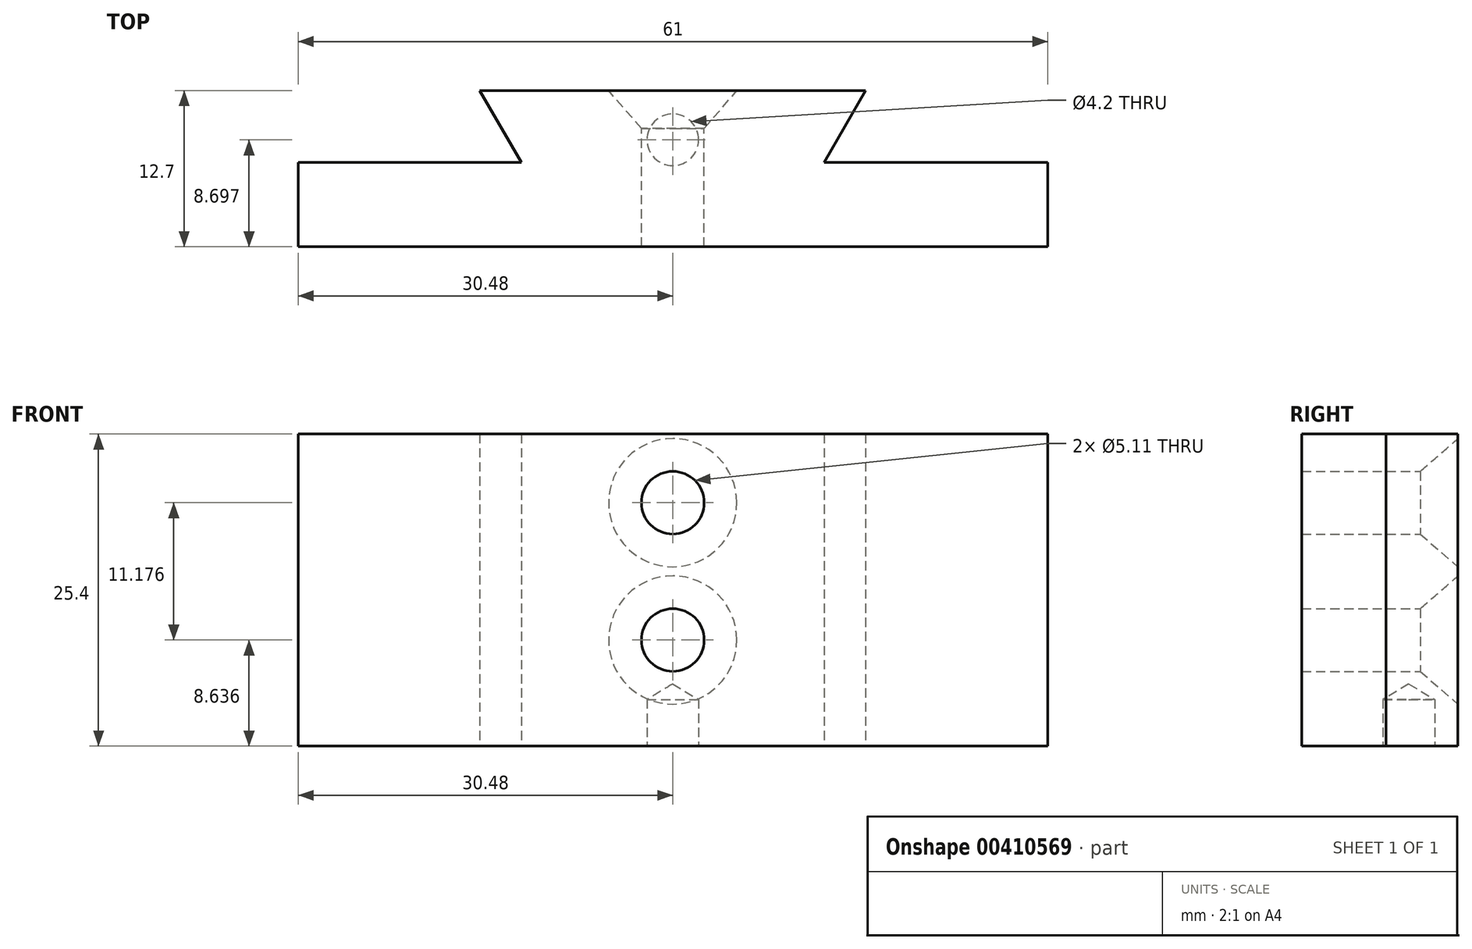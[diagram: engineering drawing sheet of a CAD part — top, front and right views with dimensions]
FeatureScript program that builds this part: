
annotation { "Feature Type Name" : "Feature", "Feature Type Description" : "" }
export const myFeature = defineFeature(function(context is Context, id is Id, definition is map)
    precondition{}
    {
        {
            var Q0;
            Q0=qCreatedBy(makeId("Top.planeOp"),FACE);
            var sketch = newSketch(context, id + "F0", { "sketchPlane" : qUnion([Q0])});
            skLineSegment(sketch, "E0", {"start": v(0, 8.03) * mm, "end": v(-15.7, 8.03) * mm});
            skLineSegment(sketch, "E1.MirrorCS", {"start": v(0, 8.03) * mm, "end": v(15.7, 8.03) * mm});
            skLineSegment(sketch, "E2", {"start": v(0, 2.19) * mm, "end": v(-30.48, 2.19) * mm});
            skLineSegment(sketch, "E3.MirrorCS", {"start": v(0, 2.19) * mm, "end": v(30.48, 2.19) * mm});
            skLineSegment(sketch, "E4", {"start": v(-15.7, 8.03) * mm, "end": v(-12.33, 2.19) * mm});
            skLineSegment(sketch, "E5.MirrorCS", {"start": v(15.7, 8.03) * mm, "end": v(12.33, 2.19) * mm});
            skLineSegment(sketch, "E6.bottom", {"start": v(-30.48, 2.19) * mm, "end": v(30.52, 2.19) * mm});
            skLineSegment(sketch, "E6.top", {"start": v(-30.48, -4.67) * mm, "end": v(30.52, -4.67) * mm});
            skLineSegment(sketch, "E6.left", {"start": v(-30.48, 2.19) * mm, "end": v(-30.48, -4.67) * mm});
            skLineSegment(sketch, "E6.right", {"start": v(30.52, 2.19) * mm, "end": v(30.52, -4.67) * mm});
            skLineSegment(sketch, "E7", {"start": v(-17.76, 4.03) * mm, "end": v(19.96, 4.03) * mm, "construction": true});
            skPoint(sketch, "E8", {"position": v(0, 4.03) * mm});
            skSolve(sketch);
        }
        {
            var Q0;
            Q0 = qSketchRegion(id + "F0", true);
            extrude(context, id + "F1", {"entities" : qUnion([Q0]), "depth" : 25.4 * mm});
        }
        {
            var Q0;
            Q0=qCreatedBy(makeId("Top.planeOp"),FACE);
            var sketch = newSketch(context, id + "F2", { "sketchPlane" : qUnion([Q0])});
            skLineSegment(sketch, "E9", {"start": v(-33.8, 4.03) * mm, "end": v(32.14, 4.03) * mm, "construction": true});
            skPoint(sketch, "E10", {"position": v(0, 4.03) * mm});
            skSolve(sketch);
        }
        {
            var Q0;
            Q0=sQuery(id+"F2.wireOp",VERTEX,"E10");
            var Q1;
            Q1=makeQuery(id+"F1.opExtrude","SWEPT_BODY",BODY,{"disambiguationData":[OSD([sQuery(id+"F0.wireOp",EDGE,"E0"),sQuery(id+"F0.wireOp",EDGE,"E1.MirrorCS"),sQuery(id+"F0.wireOp",EDGE,"E4"),sQuery(id+"F0.wireOp",EDGE,"E5.MirrorCS"),sQuery(id+"F0.wireOp",EDGE,"E6.bottom"),sQuery(id+"F0.wireOp",EDGE,"E6.top"),sQuery(id+"F0.wireOp",EDGE,"E6.left"),sQuery(id+"F0.wireOp",EDGE,"E6.right")])]});
            hole(context, id + "F3", {"style" : HoleStyle.SIMPLE, "endStyle" : HoleEndStyle.BLIND, "oppositeDirection" : true, "standardTappedOrClearance" : lookupTablePath({ "standard" : "ISO", "engagement" : "75%", "pitch" : "0.8 mm", "size" : "M5", "type" : "Tapped" }), "standardBlindInLast" : lookupTablePath({ "standard" : "ISO", "engagement" : "75%", "pitch" : "0.8 mm", "size" : "M5", "type" : "Tapped" }), "holeDiameter" : 4.2 * mm, "showTappedDepth" : true, "holeDepth" : 3.8 * mm, "isTappedThrough" : true, "tappedDepth" : 3 * mm, "tapClearance" : 1, "startFromSketch" : true, "locations" : qUnion([Q0]), "scope" : qUnion([Q1]), "majorDiameter" : 5 * mm});
        }
        {
            var Q0;
            Q0=makeQuery(id+"F1.opExtrude","SWEPT_FACE",FACE,{"disambiguationData":[OSD([sQuery(id+"F0.wireOp",EDGE,"E0"),sQuery(id+"F0.wireOp",EDGE,"E1.MirrorCS")])]});
            var sketch = newSketch(context, id + "F4", { "sketchPlane" : qUnion([Q0])});
            skLineSegment(sketch, "E11", {"start": v(-27.44, 19.81) * mm, "end": v(30.95, 19.81) * mm, "construction": true});
            skLineSegment(sketch, "E12", {"start": v(-27.44, 8.64) * mm, "end": v(34.23, 8.64) * mm, "construction": true});
            skPoint(sketch, "E13", {"position": v(0, 19.81) * mm});
            skPoint(sketch, "E14", {"position": v(0, 8.64) * mm});
            skSolve(sketch);
        }
        {
            var Q0;
            Q0=sQuery(id+"F4.wireOp",VERTEX,"E13");
            var Q1;
            Q1=makeQuery(id+"F1.opExtrude","SWEPT_BODY",BODY,{"disambiguationData":[OSD([sQuery(id+"F0.wireOp",EDGE,"E0"),sQuery(id+"F0.wireOp",EDGE,"E1.MirrorCS"),sQuery(id+"F0.wireOp",EDGE,"E4"),sQuery(id+"F0.wireOp",EDGE,"E5.MirrorCS"),sQuery(id+"F0.wireOp",EDGE,"E6.bottom"),sQuery(id+"F0.wireOp",EDGE,"E6.top"),sQuery(id+"F0.wireOp",EDGE,"E6.left"),sQuery(id+"F0.wireOp",EDGE,"E6.right")])]});
            hole(context, id + "F5", {"style" : HoleStyle.C_SINK, "endStyle" : HoleEndStyle.THROUGH, "standardTappedOrClearance" : lookupTablePath({ "standard" : "ANSI", "fit" : "Normal (ASME)", "size" : "#10", "type" : "Clearance" }), "standardBlindInLast" : lookupTablePath({ "fit" : "Free", "standard" : "ANSI", "size" : "#10", "type" : "Clearance" }), "holeDiameter" : 5.1 * mm, "cSinkDiameter" : 10.44 * mm, "cSinkAngle" : 82 * degree, "isTappedThrough" : true, "tappedDepth" : 3 * mm, "tapClearance" : 3, "startFromSketch" : true, "locations" : qUnion([Q0]), "scope" : qUnion([Q1])});
        }
        {
            var Q0;
            Q0=sQuery(id+"F4.wireOp",VERTEX,"E14");
            var Q1;
            Q1=makeQuery(id+"F1.opExtrude","SWEPT_BODY",BODY,{"disambiguationData":[OSD([sQuery(id+"F0.wireOp",EDGE,"E0"),sQuery(id+"F0.wireOp",EDGE,"E1.MirrorCS"),sQuery(id+"F0.wireOp",EDGE,"E4"),sQuery(id+"F0.wireOp",EDGE,"E5.MirrorCS"),sQuery(id+"F0.wireOp",EDGE,"E6.bottom"),sQuery(id+"F0.wireOp",EDGE,"E6.top"),sQuery(id+"F0.wireOp",EDGE,"E6.left"),sQuery(id+"F0.wireOp",EDGE,"E6.right")])]});
            hole(context, id + "F6", {"style" : HoleStyle.C_SINK, "endStyle" : HoleEndStyle.THROUGH, "standardTappedOrClearance" : lookupTablePath({ "standard" : "ANSI", "fit" : "Normal (ASME)", "size" : "#10", "type" : "Clearance" }), "standardBlindInLast" : lookupTablePath({ "fit" : "Free", "standard" : "ANSI", "size" : "#10", "type" : "Clearance" }), "holeDiameter" : 5.1 * mm, "cSinkDiameter" : 10.44 * mm, "cSinkAngle" : 82 * degree, "isTappedThrough" : true, "tappedDepth" : 3 * mm, "tapClearance" : 3, "startFromSketch" : true, "locations" : qUnion([Q0]), "scope" : qUnion([Q1])});
        }
    });
